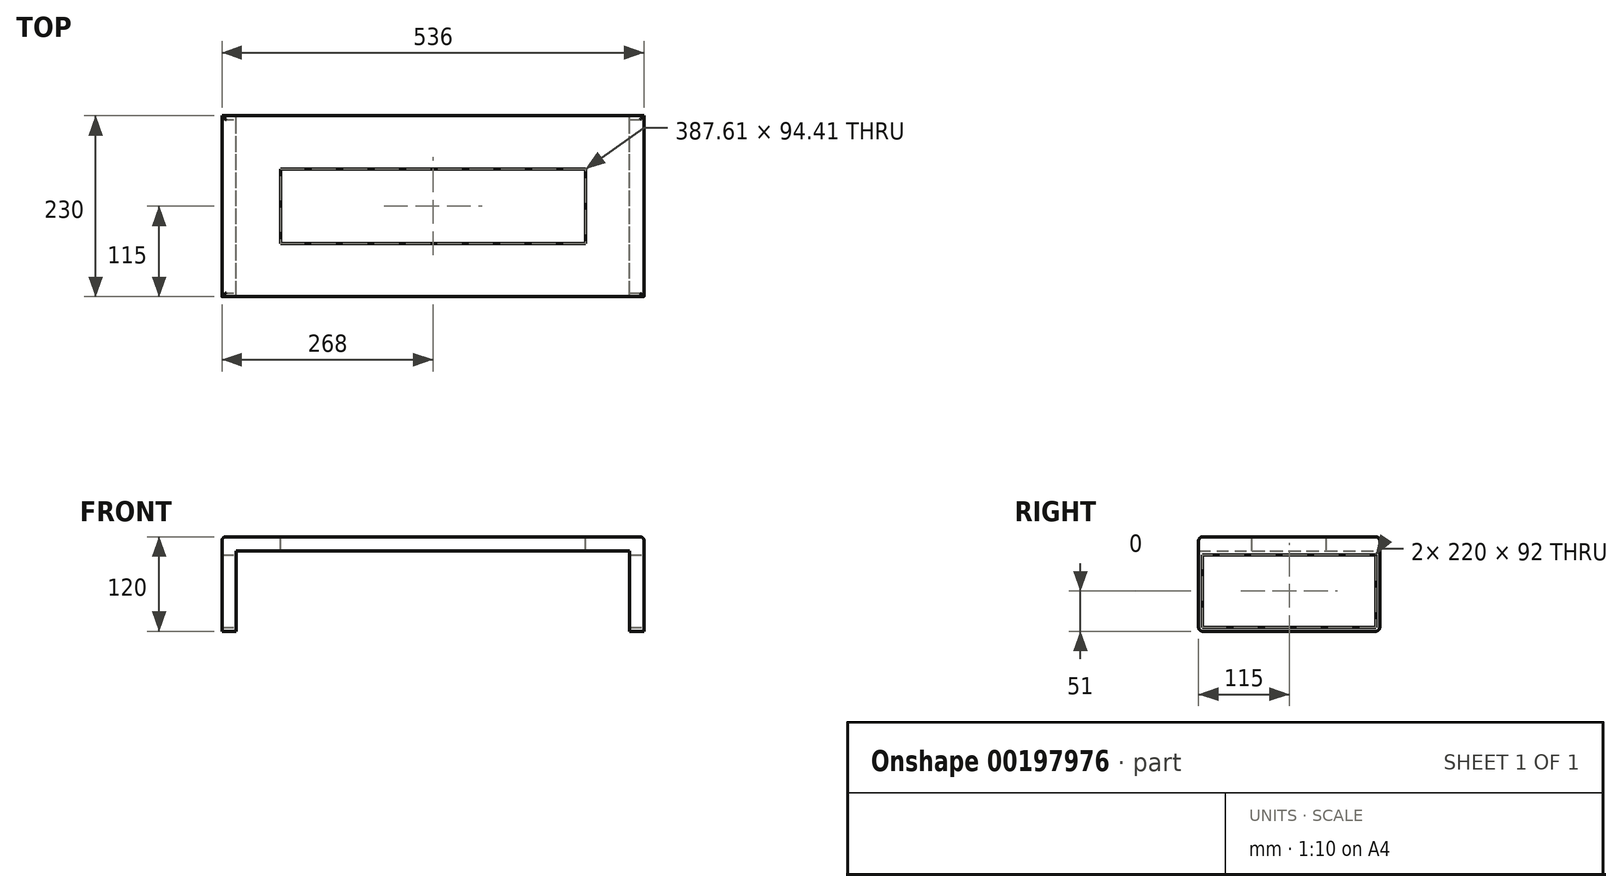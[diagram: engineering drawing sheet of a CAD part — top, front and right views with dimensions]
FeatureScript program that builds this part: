
annotation { "Feature Type Name" : "Feature", "Feature Type Description" : "" }
export const myFeature = defineFeature(function(context is Context, id is Id, definition is map)
    precondition{}
    {
        {
            var Q0;
            Q0=qCreatedBy(makeId("Front.planeOp"),FACE);
            var sketch = newSketch(context, id + "F0", { "sketchPlane" : qUnion([Q0])});
            skLineSegment(sketch, "E0.bottom", {"start": v(-250, -9) * mm, "end": v(250, -9) * mm});
            skLineSegment(sketch, "E0.top", {"start": v(-250, 9) * mm, "end": v(250, 9) * mm});
            skLineSegment(sketch, "E0.left", {"start": v(-250, -9) * mm, "end": v(-250, 9) * mm});
            skLineSegment(sketch, "E0.right", {"start": v(250, -9) * mm, "end": v(250, 9) * mm});
            skPoint(sketch, "E0.middle", {"position": v(0, 0) * mm});
            skLineSegment(sketch, "E1.bottom", {"start": v(-250, 9) * mm, "end": v(-268, 9) * mm});
            skLineSegment(sketch, "E1.top", {"start": v(-250, -111) * mm, "end": v(-268, -111) * mm});
            skLineSegment(sketch, "E1.left", {"start": v(-250, 9) * mm, "end": v(-250, -111) * mm});
            skLineSegment(sketch, "E1.right", {"start": v(-268, 9) * mm, "end": v(-268, -111) * mm});
            skLineSegment(sketch, "E2.bottom", {"start": v(250, 9) * mm, "end": v(268, 9) * mm});
            skLineSegment(sketch, "E2.top", {"start": v(250, -111) * mm, "end": v(268, -111) * mm});
            skLineSegment(sketch, "E2.left", {"start": v(250, 9) * mm, "end": v(250, -111) * mm});
            skLineSegment(sketch, "E2.right", {"start": v(268, 9) * mm, "end": v(268, -111) * mm});
            skSolve(sketch);
        }
        {
            var Q0;
            Q0 = qSketchRegion(id + "F0", true);
            extrude(context, id + "F1", {"entities" : qUnion([Q0]), "endBound" : BoundingType.SYMMETRIC, "depth" : 230 * mm});
        }
        {
            var Q0;
            Q0=qCreatedBy(makeId("Right.planeOp"),FACE);
            var sketch = newSketch(context, id + "F2", { "sketchPlane" : qUnion([Q0])});
            skLineSegment(sketch, "E3.bottom", {"start": v(-110, -14) * mm, "end": v(110, -14) * mm});
            skLineSegment(sketch, "E3.top", {"start": v(-110, -106) * mm, "end": v(110, -106) * mm});
            skLineSegment(sketch, "E3.left", {"start": v(-110, -14) * mm, "end": v(-110, -106) * mm});
            skLineSegment(sketch, "E3.right", {"start": v(110, -14) * mm, "end": v(110, -106) * mm});
            skSolve(sketch);
        }
        {
            var Q0;
            Q0 = qSketchRegion(id + "F2", true);
            extrude(context, id + "F3", {"entities" : qUnion([Q0]), "operationType" : NewBodyOperationType.REMOVE, "endBound" : BoundingType.SYMMETRIC, "oppositeDirection" : true, "depth" : 550 * mm});
        }
        {
            var Q0;
            Q0=makeQuery(id+"F1.opExtrude","CAP_EDGE",EDGE,{"disambiguationData":[OSD([sQuery(id+"F0.wireOp",EDGE,"E2.top")])],"isStart":true});
            var Q1;
            Q1=makeQuery(id+"F1.opExtrude","CAP_EDGE",EDGE,{"disambiguationData":[OSD([sQuery(id+"F0.wireOp",EDGE,"E1.top")])],"isStart":true});
            var Q2;
            Q2=makeQuery(id+"F1.opExtrude","CAP_EDGE",EDGE,{"disambiguationData":[OSD([sQuery(id+"F0.wireOp",EDGE,"E1.top")])],"isStart":false});
            var Q3;
            Q3=makeQuery(id+"F1.opExtrude","CAP_EDGE",EDGE,{"disambiguationData":[OSD([sQuery(id+"F0.wireOp",EDGE,"E2.top")])],"isStart":false});
            var Q4;
            Q4=makeQuery(id+"F1.opExtrude","CAP_EDGE",EDGE,{"disambiguationData":[OSD([sQuery(id+"F0.wireOp",EDGE,"E0.top"),sQuery(id+"F0.wireOp",EDGE,"E1.bottom"),sQuery(id+"F0.wireOp",EDGE,"E2.bottom")])],"isStart":false});
            var Q5;
            Q5=makeQuery(id+"F1.opExtrude","CAP_EDGE",EDGE,{"disambiguationData":[OSD([sQuery(id+"F0.wireOp",EDGE,"E0.top"),sQuery(id+"F0.wireOp",EDGE,"E1.bottom"),sQuery(id+"F0.wireOp",EDGE,"E2.bottom")])],"isStart":true});
            var Q6;
            Q6=makeQuery(id+"F1.opExtrude","SWEPT_EDGE",EDGE,{"disambiguationData":[OSD([sQuery(id+"F0.wireOp",EDGE,"E1.bottom"),sQuery(id+"F0.wireOp",EDGE,"E1.right")])]});
            var Q7;
            Q7=makeQuery(id+"F1.opExtrude","SWEPT_FACE",FACE,{"disambiguationData":[OSD([sQuery(id+"F0.wireOp",EDGE,"E0.top"),sQuery(id+"F0.wireOp",EDGE,"E1.bottom"),sQuery(id+"F0.wireOp",EDGE,"E2.bottom")])]});
            fillet(context, id + "F4", {"entities" : qUnion([Q0, Q1, Q2, Q3, Q4, Q5, Q6, Q7]), "radius" : 5 * mm, "tangentPropagation" : true, "allowEdgeOverflow" : false});
        }
        {
            var Q0;
            Q0=makeQuery(id+"F1.opExtrude","SWEPT_FACE",FACE,{"disambiguationData":[OSD([sQuery(id+"F0.wireOp",EDGE,"E0.top"),sQuery(id+"F0.wireOp",EDGE,"E1.bottom"),sQuery(id+"F0.wireOp",EDGE,"E2.bottom")])]});
            var sketch = newSketch(context, id + "F5", { "sketchPlane" : qUnion([Q0])});
            skLineSegment(sketch, "E4.bottom", {"start": v(193.8, -47.2) * mm, "end": v(-193.8, -47.2) * mm});
            skLineSegment(sketch, "E4.top", {"start": v(193.8, 47.2) * mm, "end": v(-193.8, 47.2) * mm});
            skLineSegment(sketch, "E4.left", {"start": v(193.8, -47.2) * mm, "end": v(193.8, 47.2) * mm});
            skLineSegment(sketch, "E4.right", {"start": v(-193.8, -47.2) * mm, "end": v(-193.8, 47.2) * mm});
            skPoint(sketch, "E4.middle", {"position": v(0, 0) * mm});
            skSolve(sketch);
        }
        {
            var Q0;
            Q0=makeQuery(id+"F5.imprint","IMPRINT",FACE,{"disambiguationData":[TD([[makeQuery(id+"F5.imprint","IMPRINT",EDGE,{"derivedFrom":sQuery(id+"F5.wireOp",EDGE,"E4.bottom")}),-1.0]])]});
            extrude(context, id + "F6", {"entities" : qUnion([Q0]), "operationType" : NewBodyOperationType.REMOVE, "endBound" : BoundingType.THROUGH_ALL, "oppositeDirection" : true, "depth" : 25 * mm});
        }
    });
